# Revit family: Domotics-DomesticRanges-GEWISS-CHORUS_COMMAND-INTERMEDIATE_SWITCH_2M
name_source: partatom
category: Apparecchi elettrici
revit_build: Autodesk Revit 2016 (Build: 20161004_0715(x64)
units: mm (PartAtom-declared; Revit-internal decimal feet)

## family parameters
Condiviso = Sì
Host = Superficie
Mantenere orientamento annotazione = Sì
Numero OmniClass = 23.80.50.11.14
Punto di calcolo locali = No
Quota connettore circolare = Usa diametro
Taglio con vuoti quando caricato = Sì
Tipo di parte = Normale
Titolo OmniClass = Switches

## types (9) — shared parameters
Bidimensionale = bidimensionale invertitori 2m : GW12103
Breaking capacity: = 1.25 In (200 position changes)
Carico apparente = 0 VA
Catalogue = DOMOTICS
Catalogue Range = CHORUS - DOMESTIC RANGE
Category = Reversing switch
Electrocod = 0130
Glow Wire Test = 850°C
IDF = 6ea41080-a751-4214-9f6a-8112c22ce85e
IDT = 886d4329-b18f-4ebd-8a86-a334d2cfd194
Immagine tipo = GW14103.jpg
Insulation resistance = > 5 MOhm
Larghezza pulsante = 46 mm  [stored 0.150919 ft]
N. poli = 1
No. Chorus modules = 2
Number of poles = 1P
Produttore = GEWISS S.p.A.
Prolonged operation (no.of position changes) = 40.000 at In 250 V ac cosÃ˜=0,6
Prospetto di default = 1219 mm
Resistance at test voltage = 2000 V at 50 Hz for 1 minute
SEO = Intermediate switch
Simbolo = SIMBOLO INVERTITORI : INV1PLUM
Standard; = EN 60669-1
Technical sheet = https://www.gewiss.com
Terminal grip on cable traction = > 50 N
Terminal tightening capacity flexible cables (mm2) = min. 0,75 - max. 2x4
Terminal tightening capacity rigid cables (mm2) = min. 0,5 - max. 2x2,5
Thermo-pressure with ball = 125
Tipo_ = CHORUS INVERTITORI 2M_BASE : GW14103 - Titanio - Illuminabile segnalazione
URL = https://www.gewiss.com
Version file RFA = 19.0
Volt = 230 V
Voltage = 250 V ac
Voltage: = 250 V ac
Wiring terminals = With screw

## per-type parameters (varying)
| type | Button key | Colour | Description: | Descrizione | EAN code | Modello | Type |
| GW12103 - Black - Illuminable | With replaceable neutral lens | Black | 1P - 16AX illuminable | REV.SWITCH, 2M 1P 16AX ILL SIG BLACK | 8011564268807 | GW12103 | Indicator |
| GW14101 - Titanium | Neutral | Titanium | 1P - 16AX | REV.SWITCH 2M 1P 16AX TITANIUM | 8011564265738 | GW14101 | General |
| GW12101 - Black | Neutral | Black | 1P - 16AX | REV.SWITCH, 2M 1P 16AX BLACK | 8011564268715 | GW12101 | General |
| GW12102 - Black - Illuminable | With diffuser | Black | 1P - 16AX illuminable | REV.SWITCH, 2M 1P 16AX ILL LOC BLACK | 8011564268760 | GW12102 | Backlit |
| GW14103 - Titanium - Illuminable | With replaceable neutral lens | Titanium | 1P - 16AX illuminable | REV.SWITCH 2M 1P 16AX ILL SIG TITANIUM | 8011564265776 | GW14103 | Indicator |
| GW10101 - White | Neutral | White | 1P - 16AX | REVERSING SWITCH, 2M 1P 16AX WHITE | 8011564259942 | GW10101 | General |
| GW10102 - White - Illuminable | With diffuser | White | 1P - 16AX illuminable | REV.SWITCH, 2M 1P 16AX ILL LOC WHITE | 8011564259966 | GW10102 | Backlit |
| GW10103 - White - Illuminable | With replaceable neutral lens | White | 1P - 16AX illuminable | REV.SWITCH, 2M 1P 16AX ILL SIG WHITE | 8011564259980 | GW10103 | Indicator |
| GW14102 - Titanium - Illuminable | With diffuser | Titanium | 1P - 16AX illuminable | REV.SWITCH 2M 1P 16AX ILL LOC TITANIUM | 8011564265752 | GW14102 | Backlit |

note: source unit labels omitted for Thermo-pressure with ball — the stored unit's dimension contradicts the parameter name (converter mislabeling)

note: [stored X ft] marks values corroborated as IEEE doubles in the binary element streams (Revit-internal decimal feet)

## geometry (parser evidence)
native form markers: Sweep x2
no freeform markers — native parametric forms only
